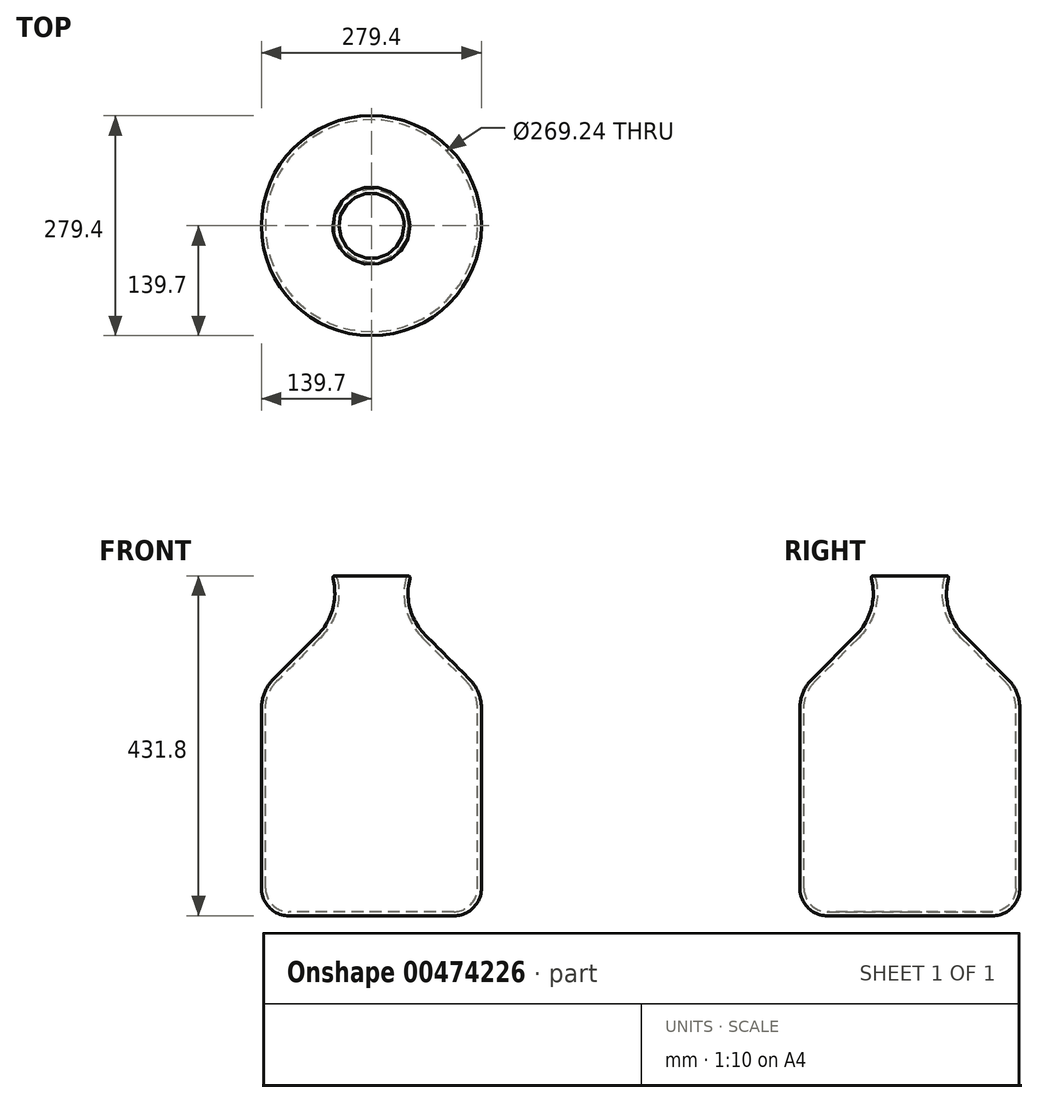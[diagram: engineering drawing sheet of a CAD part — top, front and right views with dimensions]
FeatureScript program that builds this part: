
annotation { "Feature Type Name" : "Feature", "Feature Type Description" : "" }
export const myFeature = defineFeature(function(context is Context, id is Id, definition is map)
    precondition{}
    {
        {
            var Q0;
            Q0=qCreatedBy(makeId("Front.planeOp"),FACE);
            var sketch = newSketch(context, id + "F0", { "sketchPlane" : qUnion([Q0])});
            skLineSegment(sketch, "E0", {"start": v(0, 0) * mm, "end": v(-104.75, 0) * mm});
            skLineSegment(sketch, "E1", {"start": v(0, 431.8) * mm, "end": v(-49.92, 431.8) * mm});
            skArc(sketch, "E2", {"start": v(-104.75, 0) * mm, "mid": v(-129.46, 10.24) * mm, "end": v(-139.7, 34.95) * mm});
            skLineSegment(sketch, "E3", {"start": v(-139.7, 34.95) * mm, "end": v(-139.7, 263.37) * mm});
            skArc(sketch, "E4", {"start": v(-139.7, 263.37) * mm, "mid": v(-135.65, 283.74) * mm, "end": v(-124.11, 301) * mm});
            skLineSegment(sketch, "E5", {"start": v(-124.11, 301) * mm, "end": v(-68.37, 356.75) * mm});
            skArc(sketch, "E6", {"start": v(-68.37, 356.75) * mm, "mid": v(-48.67, 391.7) * mm, "end": v(-49.92, 431.8) * mm});
            skLineSegment(sketch, "E7", {"start": v(0, 431.8) * mm, "end": v(0, 0) * mm});
            skSolve(sketch);
        }
        {
            var Q0;
            Q0 = qSketchRegion(id + "F0", true);
            var Q1;
            Q1=sQuery(id+"F0.wireOp",EDGE,"E7");
            revolve(context, id + "F1", {"entities" : qUnion([Q0]), "axis" : qUnion([Q1]), "revolveType" : RevolveType.FULL});
        }
        {
            var Q0;
            Q0=makeQuery(id+"F1.opRevolve","SWEPT_FACE",FACE,{"disambiguationData":[OSD([sQuery(id+"F0.wireOp",EDGE,"E1")])]});
            shell(context, id + "F2", {"entities" : qUnion([Q0]), "thickness" : 5.08 * mm});
        }
        {
            var Q0;
            Q0=makeQuery(id+"F1.opRevolve","SWEPT_EDGE",EDGE,{"disambiguationData":[OSD([sQuery(id+"F0.wireOp",EDGE,"E1"),sQuery(id+"F0.wireOp",EDGE,"E6")])]});
            var Q1;
            Q1=makeQuery(id+"F2.opShell","OFFSET_EDGE",EDGE,{"disambiguationData":[OSD([sQuery(id+"F0.wireOp",EDGE,"E1"),sQuery(id+"F0.wireOp",EDGE,"E6")])]});
            fillet(context, id + "F3", {"entities" : qUnion([Q0, Q1]), "radius" : 2.54 * mm, "tangentPropagation" : true, "allowEdgeOverflow" : false});
        }
    });
